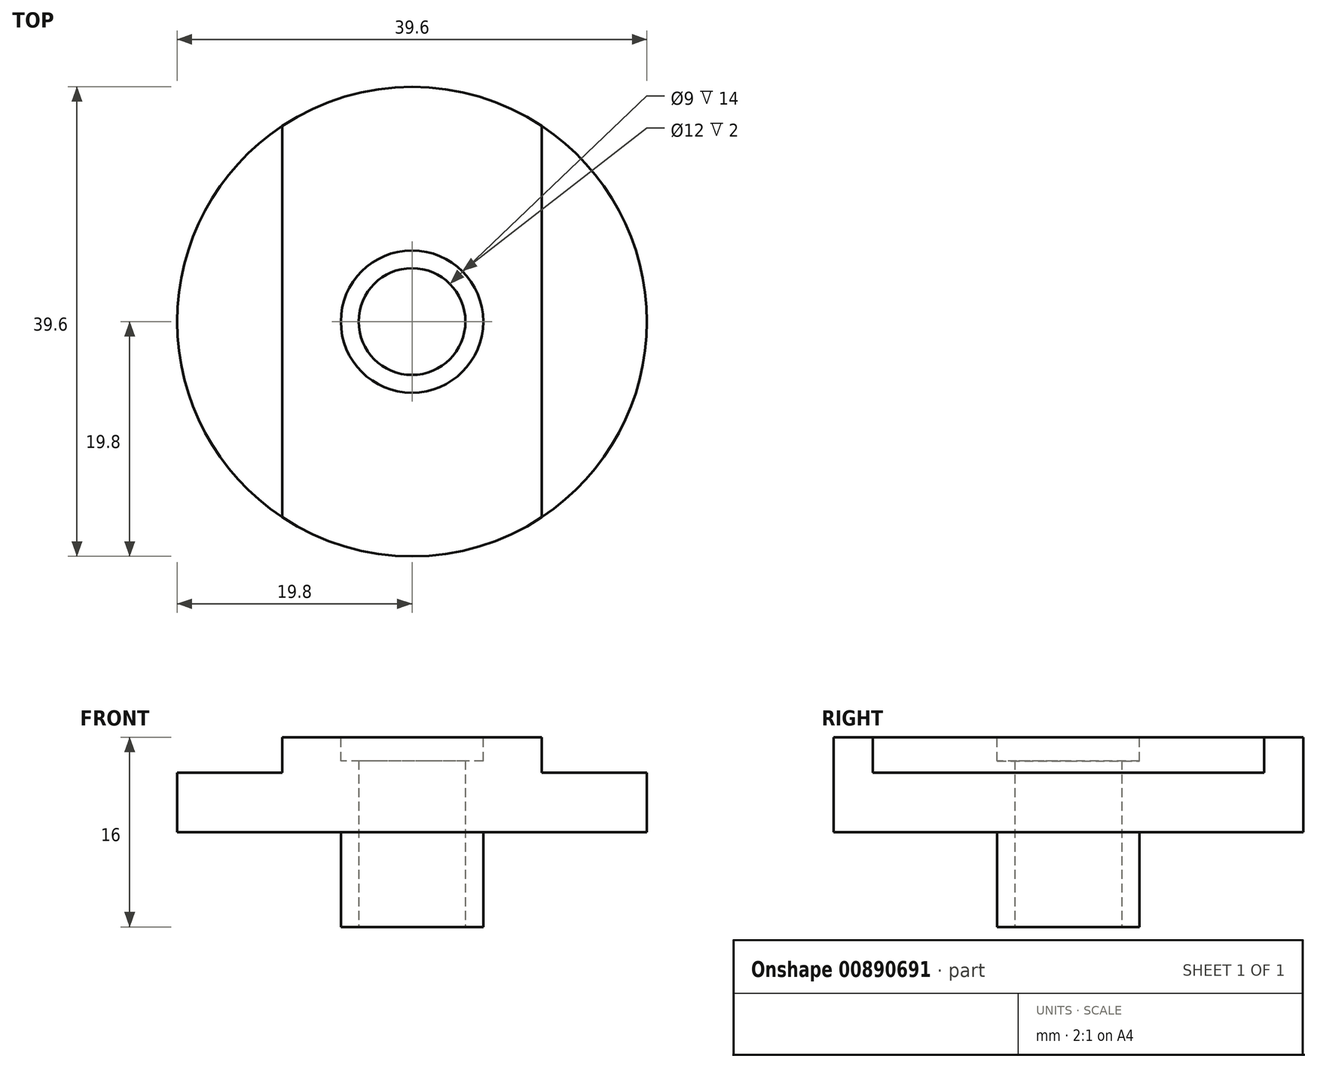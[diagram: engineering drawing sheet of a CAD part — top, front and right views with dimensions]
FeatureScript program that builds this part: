
annotation { "Feature Type Name" : "Feature", "Feature Type Description" : "" }
export const myFeature = defineFeature(function(context is Context, id is Id, definition is map)
    precondition{}
    {
        {
            var Q0;
            Q0=qCreatedBy(makeId("Top.planeOp"),FACE);
            var sketch = newSketch(context, id + "F0", { "sketchPlane" : qUnion([Q0])});
            skCircle(sketch, "E0", {"center": v(0, 0) * mm, "radius": 19.8 * mm});
            skSolve(sketch);
        }
        {
            var Q0;
            Q0 = qSketchRegion(id + "F0", true);
            extrude(context, id + "F1", {"entities" : qUnion([Q0]), "depth" : 16 * mm, "offsetDistance" : 25.4 * mm});
        }
        {
            var Q0;
            Q0=makeQuery(id+"F1.opExtrude","CAP_FACE",FACE,{"disambiguationData":[OSD([sQuery(id+"F0.wireOp",EDGE,"E0")])],"isStart":false});
            var sketch = newSketch(context, id + "F2", { "sketchPlane" : qUnion([Q0])});
            skLineSegment(sketch, "E1", {"start": v(0, 19.8) * mm, "end": v(0, -19.8) * mm, "construction": true});
            skLineSegment(sketch, "E2", {"start": v(-19.8, 0) * mm, "end": v(19.8, 0) * mm, "construction": true});
            skLineSegment(sketch, "E3.bottom", {"start": v(-10.95, 612) * mm, "end": v(10.95, 612) * mm});
            skLineSegment(sketch, "E3.top", {"start": v(-10.95, -647.05) * mm, "end": v(10.95, -647.05) * mm});
            skLineSegment(sketch, "E3.left", {"start": v(-10.95, 612) * mm, "end": v(-10.95, -647.05) * mm});
            skLineSegment(sketch, "E3.right", {"start": v(10.95, 612) * mm, "end": v(10.95, -647.05) * mm});
            skSolve(sketch);
        }
        {
            var Q0;
            {var subQ0=sQuery(id+"F2.wireOp",EDGE,"E3.left");var subQ1=makeQuery(id+"F1.opExtrude","CAP_EDGE",EDGE,{"disambiguationData":[OSD([sQuery(id+"F0.wireOp",EDGE,"E0")])],"isStart":false});var subQ2=makeQuery(id+"F2.imprint","INTERSECT",VERTEX,{"disambiguationData":[OD(0.0)],"derivedFrom":[subQ1,subQ0]});Q0=makeQuery(id+"F2.imprint","IMPRINT",FACE,{"disambiguationData":[TD([[makeQuery(id+"F2.imprint","IMPRINT",EDGE,{"disambiguationData":[TD([[subQ2,-1.0]])],"derivedFrom":subQ0}),-1.0]])]});}
            var Q1;
            {var subQ0=sQuery(id+"F2.wireOp",EDGE,"E3.right");var subQ1=makeQuery(id+"F1.opExtrude","CAP_EDGE",EDGE,{"disambiguationData":[OSD([sQuery(id+"F0.wireOp",EDGE,"E0")])],"isStart":false});var subQ2=makeQuery(id+"F2.imprint","INTERSECT",VERTEX,{"disambiguationData":[OD(0.0)],"derivedFrom":[subQ1,subQ0]});Q1=makeQuery(id+"F2.imprint","IMPRINT",FACE,{"disambiguationData":[TD([[makeQuery(id+"F2.imprint","IMPRINT",EDGE,{"disambiguationData":[TD([[subQ2,-1.0]])],"derivedFrom":subQ0}),1.0]])]});}
            extrude(context, id + "F3", {"entities" : qUnion([Q0, Q1]), "operationType" : NewBodyOperationType.REMOVE, "oppositeDirection" : true, "depth" : 3 * mm, "offsetDistance" : 25.4 * mm});
        }
        {
            var Q0;
            Q0=makeQuery(id+"F1.opExtrude","CAP_FACE",FACE,{"disambiguationData":[OSD([sQuery(id+"F0.wireOp",EDGE,"E0")])],"isStart":true});
            var sketch = newSketch(context, id + "F4", { "sketchPlane" : qUnion([Q0])});
            skCircle(sketch, "E4", {"center": v(0, 0) * mm, "radius": 6 * mm});
            skSolve(sketch);
        }
        {
            var Q0;
            Q0=makeQuery(id+"F4.imprint","IMPRINT",FACE,{"disambiguationData":[TD([[makeQuery(id+"F4.imprint","IMPRINT",EDGE,{"derivedFrom":sQuery(id+"F4.wireOp",EDGE,"E4")}),-1.0]])]});
            extrude(context, id + "F5", {"entities" : qUnion([Q0]), "operationType" : NewBodyOperationType.REMOVE, "oppositeDirection" : true, "depth" : 8 * mm, "offsetDistance" : 25.4 * mm});
        }
        {
            var Q0;
            Q0=makeQuery(id+"F1.opExtrude","CAP_FACE",FACE,{"disambiguationData":[OSD([sQuery(id+"F0.wireOp",EDGE,"E0")])],"isStart":true});
            var sketch = newSketch(context, id + "F6", { "sketchPlane" : qUnion([Q0])});
            skPoint(sketch, "E5", {"position": v(0, 0) * mm});
            skSolve(sketch);
        }
        {
            var Q0;
            Q0=sQuery(id+"F6.wireOp",VERTEX,"E5");
            var Q1;
            Q1=makeQuery(id+"F1.opExtrude","SWEPT_BODY",BODY,{"disambiguationData":[OSD([sQuery(id+"F0.wireOp",EDGE,"E0")])]});
            hole(context, id + "F7", {"style" : HoleStyle.SIMPLE, "endStyle" : HoleEndStyle.THROUGH, "standardTappedOrClearance" : lookupTablePath({ "fit" : "Normal", "standard" : "ISO", "size" : "M8", "type" : "Clearance" }), "standardBlindInLast" : lookupTablePath({ "fit" : "Normal", "standard" : "ISO", "size" : "M8", "type" : "Clearance" }), "holeDiameter" : 9 * mm, "majorDiameter" : 10 * mm, "isTappedThrough" : true, "tappedDepth" : 12.7 * mm, "tapClearance" : 3, "locations" : qUnion([Q0]), "scope" : qUnion([Q1])});
        }
        {
            var Q0;
            Q0=makeQuery(id+"F1.opExtrude","CAP_FACE",FACE,{"disambiguationData":[OSD([sQuery(id+"F0.wireOp",EDGE,"E0")])],"isStart":false});
            var sketch = newSketch(context, id + "F8", { "sketchPlane" : qUnion([Q0])});
            skCircle(sketch, "E6", {"center": v(0, 0) * mm, "radius": 6 * mm});
            skSolve(sketch);
        }
        {
            var Q0;
            Q0=makeQuery(id+"F8.imprint","IMPRINT",FACE,{"disambiguationData":[TD([[makeQuery(id+"F8.imprint","IMPRINT",EDGE,{"derivedFrom":sQuery(id+"F8.wireOp",EDGE,"E6")}),1.0]])]});
            extrude(context, id + "F9", {"entities" : qUnion([Q0]), "operationType" : NewBodyOperationType.REMOVE, "oppositeDirection" : true, "depth" : 2 * mm, "offsetDistance" : 25 * mm});
        }
    });
